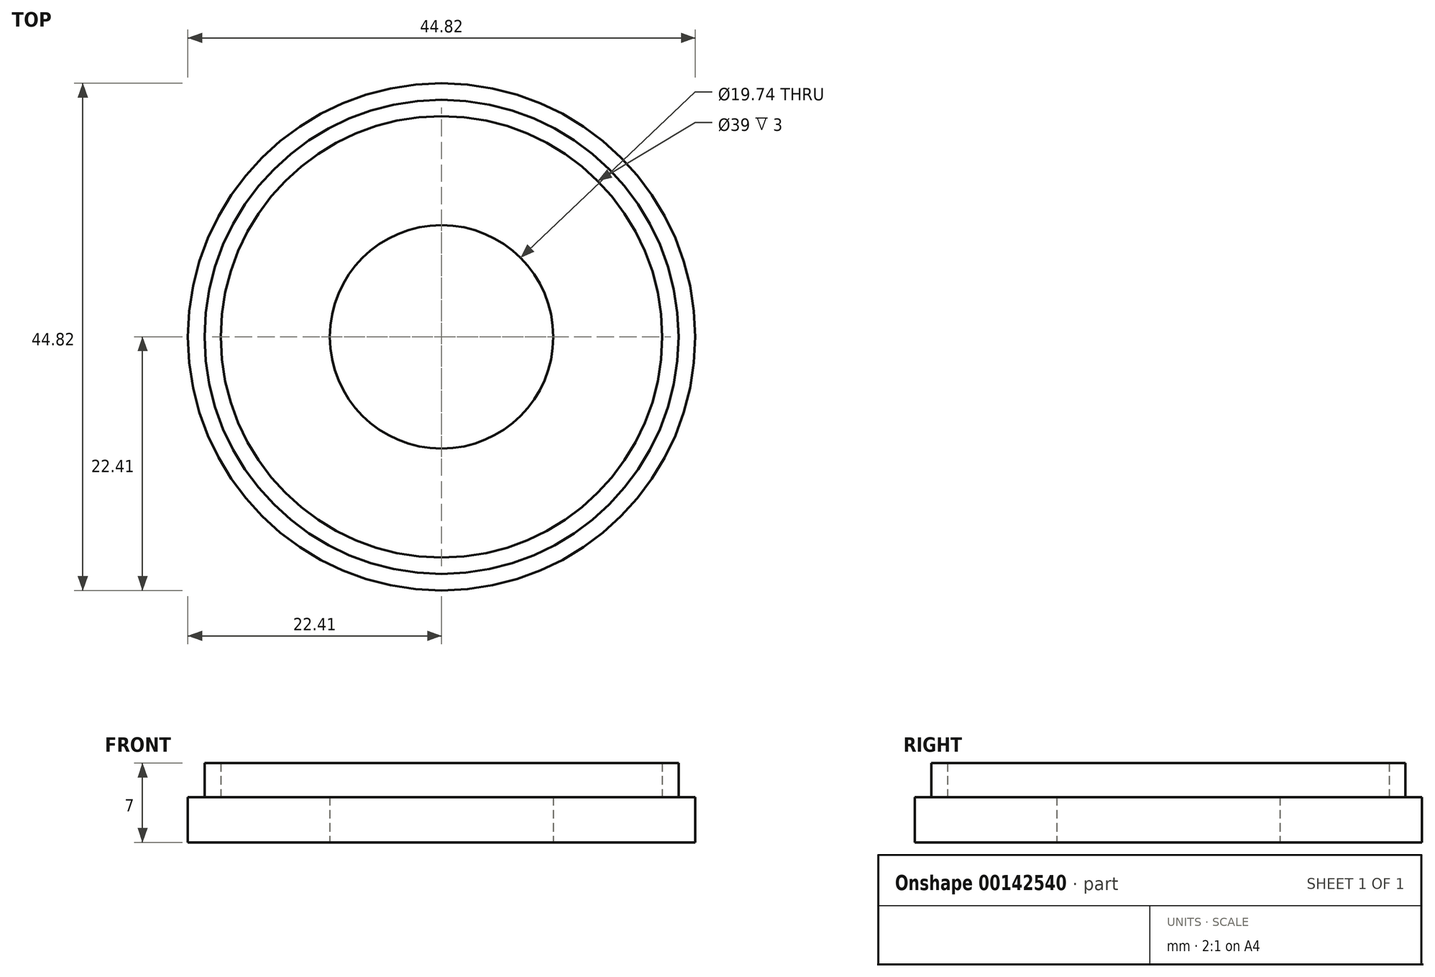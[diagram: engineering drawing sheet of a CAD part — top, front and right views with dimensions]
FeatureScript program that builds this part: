
annotation { "Feature Type Name" : "Feature", "Feature Type Description" : "" }
export const myFeature = defineFeature(function(context is Context, id is Id, definition is map)
    precondition{}
    {
        {
            var Q0;
            Q0=qCreatedBy(makeId("Top.planeOp"),FACE);
            var sketch = newSketch(context, id + "F0", { "sketchPlane" : qUnion([Q0])});
            skCircle(sketch, "E0", {"center": v(0, 0) * mm, "radius": 9.87 * mm});
            skCircle(sketch, "E1", {"center": v(0, 0) * mm, "radius": 20.94 * mm});
            skCircle(sketch, "E2", {"center": v(0, 0) * mm, "radius": 22.41 * mm});
            skCircle(sketch, "E3", {"center": v(0, 0) * mm, "radius": 19.5 * mm});
            skSolve(sketch);
        }
        {
            var Q0;
            Q0=makeQuery(id+"F0.imprint","IMPRINT",FACE,{"disambiguationData":[TD([[makeQuery(id+"F0.imprint","IMPRINT",EDGE,{"derivedFrom":sQuery(id+"F0.wireOp",EDGE,"E0")}),-1.0]])]});
            var Q1;
            Q1=makeQuery(id+"F0.imprint","IMPRINT",FACE,{"disambiguationData":[TD([[makeQuery(id+"F0.imprint","IMPRINT",EDGE,{"derivedFrom":sQuery(id+"F0.wireOp",EDGE,"E1")}),1.0]])]});
            var Q2;
            Q2=makeQuery(id+"F0.imprint","IMPRINT",FACE,{"disambiguationData":[TD([[makeQuery(id+"F0.imprint","IMPRINT",EDGE,{"derivedFrom":sQuery(id+"F0.wireOp",EDGE,"E1")}),-1.0]])]});
            extrude(context, id + "F1", {"entities" : qUnion([Q0, Q1, Q2]), "depth" : 4 * mm});
        }
        {
            var Q0;
            Q0=makeQuery(id+"F0.imprint","IMPRINT",FACE,{"disambiguationData":[TD([[makeQuery(id+"F0.imprint","IMPRINT",EDGE,{"derivedFrom":sQuery(id+"F0.wireOp",EDGE,"E1")}),1.0]])]});
            extrude(context, id + "F2", {"entities" : qUnion([Q0]), "operationType" : NewBodyOperationType.ADD, "depth" : 7 * mm});
        }
    });
